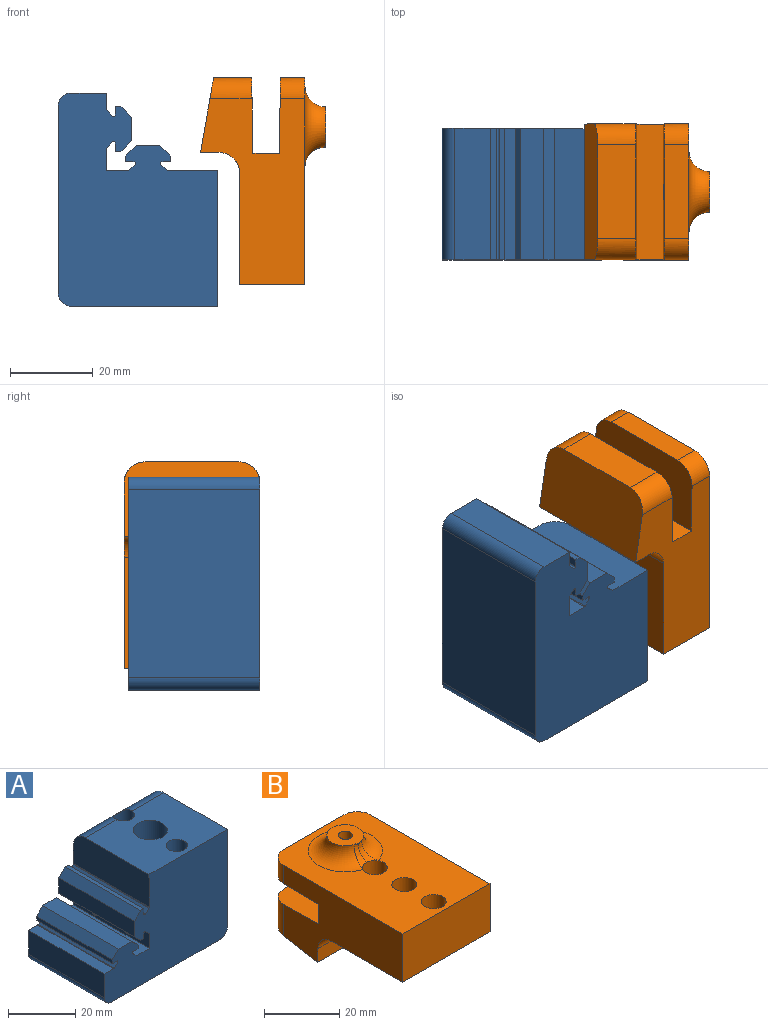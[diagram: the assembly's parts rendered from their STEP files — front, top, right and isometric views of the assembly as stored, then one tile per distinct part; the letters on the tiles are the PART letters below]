
ASSEMBLY  parts=2 mates=1
PART A: 56 faces, bbox 51.6x31.8x38.5 mm
  f0: cylinder r=3.17mm len=6.35mm, axis (0,0,1), area 51.2mm2, adj f2,f55
  f1: plane 32.85x26.67mm, normal (0,0,1), area 749.6mm2, adj f6,f8,f13,f14,f24,f53,f54
  f2: plane 21.43x11.36mm, normal (0,0,-1), area 161.5mm2, adj f0,f4,f5,f7,f14,f21,f22
  f3: plane 21.43x11.36mm, normal (0,0,1), area 193.2mm2, adj f4,f5,f7,f10,f21,f22
  f4: plane 18.15x5.81mm, normal (-1,0,0), area 105.4mm2, adj f2,f3,f7,f22
  f5: plane 18.15x5.81mm, normal (1,0,0), area 105.4mm2, adj f2,f3,f7,f21
  f6: plane 51.56x38.48mm, normal (0,-1,0), area 1580.6mm2, adj f1,f8,f11,f15,f16,f17,f18,f19
  f7: plane 51.56x33.4mm, normal (0,1,0), area 1347.8mm2, adj f2,f3,f4,f5,f8,f11,f15,f16
  f8: plane 35.48x31.75mm, normal (1,0,0), area 1098.2mm2, adj f1,f6,f7,f19,f20,f23,f24
  f9: plane 6.35x6.35mm, normal (0,0,1), area 31.7mm2, adj f10
  f10: cylinder r=3.17mm len=6.35mm, axis (0,0,1), area 54.6mm2, adj f3,f9
  f11: plane 45.56x31.75mm, normal (0,0,-1), area 1446.4mm2, adj f6,f7,f18,f19
  f12: plane 6.35x6.35mm, normal (0,0,1), area 31.7mm2, adj f13
  f13: cylinder r=3.17mm len=10.51mm, axis (0,0,1), area 209.6mm2, adj f1,f12
  f14: cylinder r=3.17mm len=10.51mm, axis (0,0,1), area 202.6mm2, adj f1,f2,f24
  f15: plane 31.75x8.68mm, normal (-1,0,0), area 275.7mm2, adj f6,f7,f17,f18
  f16: cylinder r=0.25mm len=31.75mm, axis (0,-1,0), area 6.2mm2, adj f6,f7,f17,f25
  f17: plane 31.75x3.83mm, normal (0,0,1), area 121.4mm2, adj f6,f7,f15,f16
  f18: cylinder r=3mm len=31.75mm, axis (0,-1,0), area 149.6mm2, adj f6,f7,f11,f15
  f19: cylinder r=3mm len=31.75mm, axis (0,-1,0), area 149.6mm2, adj f6,f7,f8,f11
  f20: cylinder r=1.9mm len=32.76mm, axis (1,0,0), area 390.8mm2, adj f8,f38
  f21: plane 5.81x5.68mm, normal (0.5,0.87,0), area 38.1mm2, adj f2,f3,f5,f22
  f22: plane 5.81x5.68mm, normal (-0.5,0.87,0), area 38.1mm2, adj f2,f3,f4,f21
  f23: cylinder r=1.9mm len=32.76mm, axis (1,0,0), area 390.8mm2, adj f8,f38
  f24: cylinder r=5.08mm len=32.85mm, axis (-1,0,0), area 242.8mm2, adj f1,f7,f8,f14,f53
  f25: plane 31.75x0.07mm, normal (0.71,0,0.71), area 3.2mm2, adj f6,f7,f16,f44
  f26: plane 31.75x1.5mm, normal (-0.71,0,-0.71), area 67.4mm2, adj f6,f7,f39,f49
  f27: plane 31.75x1.36mm, normal (0,0,1), area 43.1mm2, adj f6,f7,f30,f50
  f28: cylinder r=0.35mm len=31.75mm, axis (0,-1,0), area 26.2mm2, adj f6,f7,f30,f48
  f29: plane 31.75x1.36mm, normal (0,0,-1), area 43.1mm2, adj f6,f7,f32,f41
  f30: plane 31.75x2.05mm, normal (1,0,0), area 65.1mm2, adj f6,f7,f27,f28
  f31: cylinder r=0.35mm len=31.75mm, axis (0,-1,0), area 26.2mm2, adj f6,f7,f34,f42
  f32: plane 31.75x2.05mm, normal (1,0,0), area 65.1mm2, adj f6,f7,f29,f49
  f33: plane 31.75x2.62mm, normal (0.71,0,0.7), area 117mm2, adj f6,f7,f36,f47
  f34: plane 31.75x2.05mm, normal (0,0,-1), area 65.1mm2, adj f6,f7,f31,f47
  f35: cylinder r=0.35mm len=31.75mm, axis (0,-1,0), area 8.7mm2, adj f6,f7,f48,f53
  f36: plane 31.75x5.67mm, normal (0,0,1), area 179.9mm2, adj f6,f7,f33,f40
  f37: cylinder r=0.35mm len=31.75mm, axis (0,-1,0), area 26.2mm2, adj f6,f7,f44,f46
  f38: plane 31.75x5.23mm, normal (-1,0,0), area 143.2mm2, adj f6,f7,f20,f23,f39,f43
  f39: cylinder r=0.35mm len=31.75mm, axis (0,-1,0), area 8.7mm2, adj f6,f7,f26,f38
  f40: plane 31.75x2.62mm, normal (-0.71,0,0.7), area 117mm2, adj f6,f7,f36,f51
  f41: plane 31.75x2.62mm, normal (-0.7,0,-0.71), area 117mm2, adj f6,f7,f29,f45
  f42: plane 31.75x1.5mm, normal (0.71,0,0.71), area 67.4mm2, adj f6,f7,f31,f52
  f43: plane 31.75x5.23mm, normal (0,0,1), area 165.9mm2, adj f6,f7,f38,f52
  f44: plane 31.75x1.5mm, normal (-0.71,0,0.71), area 67.4mm2, adj f6,f7,f25,f37
  f45: plane 31.75x5.67mm, normal (-1,0,0), area 179.9mm2, adj f6,f7,f41,f50
  f46: plane 31.75x2.05mm, normal (0,0,-1), area 65.1mm2, adj f6,f7,f37,f51
  f47: plane 31.75x1.36mm, normal (1,0,0), area 43.1mm2, adj f6,f7,f33,f34
  f48: plane 31.75x1.5mm, normal (-0.71,0,0.71), area 67.4mm2, adj f6,f7,f28,f35
  f49: cylinder r=0.35mm len=31.75mm, axis (0,-1,0), area 26.2mm2, adj f6,f7,f26,f32
  f50: plane 31.75x2.62mm, normal (-0.7,0,0.71), area 117mm2, adj f6,f7,f27,f45
  f51: plane 31.75x1.36mm, normal (-1,0,0), area 43.1mm2, adj f6,f7,f40,f46
  f52: cylinder r=0.35mm len=31.75mm, axis (0,-1,0), area 8.7mm2, adj f6,f7,f42,f43
  f53: plane 31.77x11.94mm, normal (-1,0,-0.01), area 372.9mm2, adj f1,f6,f7,f24,f35
  f54: cylinder r=5.08mm len=10.16mm, axis (0,0,1), area 253.4mm2, adj f1,f55
  f55: plane 10.16x10.16mm, normal (0,0,1), area 49.4mm2, adj f0,f54
PART B: 28 faces, bbox 33.2x53x34.2 mm
  f0: plane 32.86x26.92mm, normal (0,0,-1), area 752.5mm2, adj f4,f5,f6,f7,f8,f25,f26
  f1: cylinder r=3.3mm len=7.81mm, axis (0,0,1), area 162mm2, adj f9,f27
  f2: bspline ~5x4.79mm, area 11.3mm2, adj f6,f21,f23,f24
  f3: plane 32.86x6.35mm, normal (0,1,0), area 208.6mm2, adj f4,f5,f10,f12
  f4: plane 44.96x25.27mm, normal (1,0,0), area 735.2mm2, adj f0,f3,f8,f9,f10,f12,f14,f16
  f5: plane 44.96x25.27mm, normal (-1,0,0), area 735.2mm2, adj f0,f3,f8,f9,f10,f12,f15,f17
  f6: cylinder r=3.3mm len=17.03mm, axis (0,0,-1), area 333.2mm2, adj f0,f2,f9,f24,f25
  f7: cylinder r=3.3mm len=15.75mm, axis (0,0,-1), area 326.7mm2, adj f0,f9
  f8: plane 32.86x15.75mm, normal (0,-1,0), area 517.4mm2, adj f0,f4,f5,f9
  f9: plane 50.04x32.86mm, normal (0,0,1), area 1230.8mm2, adj f1,f4,f5,f6,f7,f8,f13,f14
  f10: plane 32.89x18.33mm, normal (0,0.02,1), area 589.9mm2, adj f3,f4,f5,f11,f16,f17
  f11: plane 22.7x9.2mm, normal (0,1,0), area 208.8mm2, adj f10,f16,f17,f20
  f12: plane 32.95x18.38mm, normal (0,0.02,-1), area 578.6mm2, adj f3,f4,f5,f13,f14,f15,f18
  f13: plane 22.7x5.9mm, normal (0,1,0), area 134mm2, adj f9,f12,f14,f15
  f14: cylinder r=5.08mm len=5.99mm, axis (0,0,-1), area 47.5mm2, adj f4,f9,f12,f13
  f15: cylinder r=5.08mm len=5.99mm, axis (0,0,1), area 47.5mm2, adj f5,f9,f12,f13
  f16: cylinder r=5.08mm len=10.18mm, axis (0,0,1), area 77.3mm2, adj f4,f10,f11,f20
  f17: cylinder r=5.08mm len=10.18mm, axis (0,0,-1), area 77.3mm2, adj f5,f10,f11,f20
  f18: cylinder r=1.9mm len=11.11mm, axis (0,0,1), area 132.4mm2, adj f12,f22
  f19: plane 32.86x4.45mm, normal (0,-1,0), area 146mm2, adj f4,f5,f20,f25
  f20: plane 33.23x18.41mm, normal (0,0.17,-0.98), area 590.6mm2, adj f4,f5,f11,f16,f17,f19
  f21: cylinder r=4.9mm len=2.84mm, axis (0,0,-1), area 0.7mm2, adj f2,f22,f24
  f22: plane 9.8x9.8mm, normal (0,0,1), area 64.1mm2, adj f18,f21,f23
  f23: torus R=9.9mm, axis (0,0,1), area 300.4mm2, adj f2,f9,f22,f24
  f24: bspline ~5x4.79mm, area 11.7mm2, adj f2,f6,f21,f23
  f25: cylinder r=5.08mm len=32.86mm, axis (1,0,0), area 243.4mm2, adj f0,f4,f5,f6,f19
  f26: cylinder r=5.08mm len=10.16mm, axis (0,0,-1), area 253.4mm2, adj f0,f27
  f27: plane 10.16x10.16mm, normal (0,0,-1), area 46.8mm2, adj f1,f26
PLACE A rot(axis=(0,1,0),90deg) t=(78.95,17.85,6.67)mm
PLACE B rot(axis=(0.58,0.58,0.58),120deg) t=(84.39,18.4,11.31)mm
MATE planar B.f5 <-> A.f6  axis (0,-1,0) through (96.3,1.98,18.41)mm
